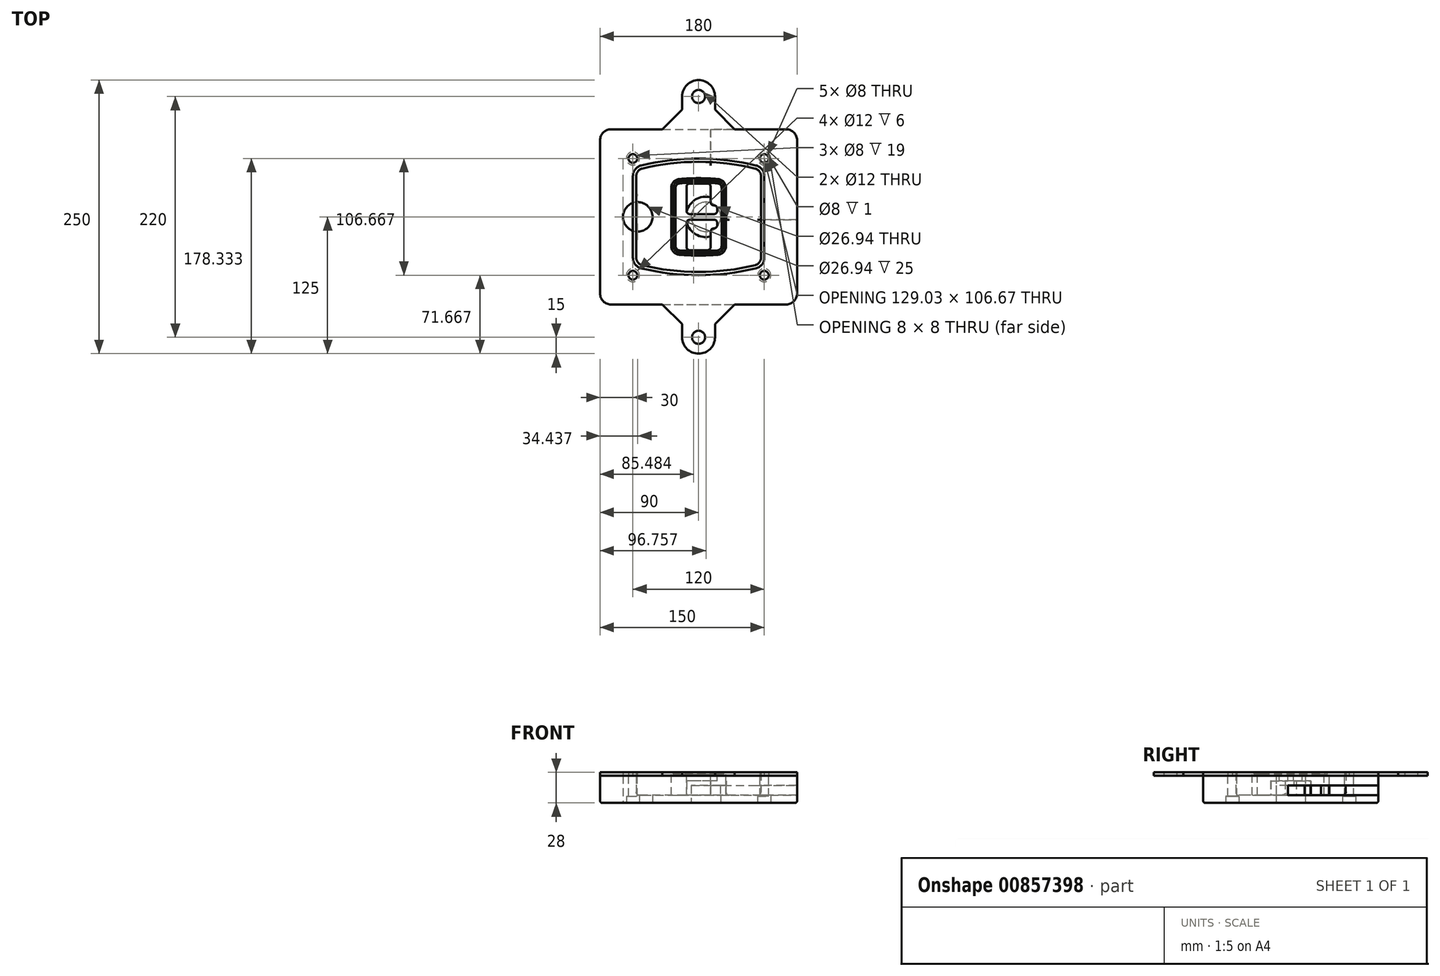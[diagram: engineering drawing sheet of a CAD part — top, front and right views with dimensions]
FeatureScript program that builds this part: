
annotation { "Feature Type Name" : "Feature", "Feature Type Description" : "" }
export const myFeature = defineFeature(function(context is Context, id is Id, definition is map)
    precondition{}
    {
        {
            var Q0;
            Q0=qCreatedBy(makeId("Top.planeOp"),FACE);
            var sketch = newSketch(context, id + "F0", { "sketchPlane" : qUnion([Q0])});
            skPoint(sketch, "E0.rect.middle", {"position": v(0, 0) * mm});
            skLineSegment(sketch, "E1.bottom", {"start": v(-80, -80) * mm, "end": v(80, -80) * mm});
            skLineSegment(sketch, "E1.top", {"start": v(-80, 80) * mm, "end": v(80, 80) * mm});
            skLineSegment(sketch, "E1.left", {"start": v(-90, -70) * mm, "end": v(-90, 70) * mm});
            skLineSegment(sketch, "E1.right", {"start": v(90, -70) * mm, "end": v(90, 70) * mm});
            skLineSegment(sketch, "E2", {"start": v(-90, 80) * mm, "end": v(90, -80) * mm, "construction": true});
            skLineSegment(sketch, "E3", {"start": v(90, 80) * mm, "end": v(-90, -80) * mm, "construction": true});
            skCircle(sketch, "E4", {"center": v(-60, 53.33) * mm, "radius": 4 * mm});
            skCircle(sketch, "E5", {"center": v(60, 53.33) * mm, "radius": 4 * mm});
            skCircle(sketch, "E6", {"center": v(60, -53.33) * mm, "radius": 4 * mm});
            skCircle(sketch, "E7", {"center": v(-60, -53.33) * mm, "radius": 4 * mm});
            skLineSegment(sketch, "E8", {"start": v(-60, 53.33) * mm, "end": v(60, 53.33) * mm, "construction": true});
            skLineSegment(sketch, "E9", {"start": v(60, 53.33) * mm, "end": v(60, -53.33) * mm, "construction": true});
            skLineSegment(sketch, "E10", {"start": v(60, -53.33) * mm, "end": v(-60, -53.33) * mm, "construction": true});
            skLineSegment(sketch, "E11", {"start": v(-60, -53.33) * mm, "end": v(-60, 53.33) * mm, "construction": true});
            skLineSegment(sketch, "E12", {"start": v(-60, 37.3) * mm, "end": v(-60, -37.3) * mm});
            skLineSegment(sketch, "E13", {"start": v(60, 37.3) * mm, "end": v(60, -37.3) * mm});
            skArc(sketch, "E14", {"start": v(52.38, 47.01) * mm, "mid": v(0, 53.33) * mm, "end": v(-52.38, 47.01) * mm});
            skArc(sketch, "E15", {"start": v(-52.38, -47.01) * mm, "mid": v(0, -53.33) * mm, "end": v(52.38, -47.01) * mm});
            skLineSegment(sketch, "E16", {"start": v(-60, 0) * mm, "end": v(60, 0) * mm, "construction": true});
            skPoint(sketch, "E17.visualSharp", {"position": v(-60, -45) * mm});
            skArc(sketch, "E17.filletArc", {"start": v(-60, -37.3) * mm, "mid": v(-57.87, -43.47) * mm, "end": v(-52.38, -47.01) * mm});
            skPoint(sketch, "E18.visualSharp", {"position": v(-60, 45) * mm});
            skArc(sketch, "E18.filletArc", {"start": v(-52.38, 47.01) * mm, "mid": v(-57.87, 43.47) * mm, "end": v(-60, 37.3) * mm});
            skPoint(sketch, "E19.visualSharp", {"position": v(60, 45) * mm});
            skArc(sketch, "E19.filletArc", {"start": v(60, 37.3) * mm, "mid": v(57.87, 43.47) * mm, "end": v(52.38, 47.01) * mm});
            skPoint(sketch, "E20.visualSharp", {"position": v(60, -45) * mm});
            skArc(sketch, "E20.filletArc", {"start": v(52.38, -47.01) * mm, "mid": v(57.87, -43.47) * mm, "end": v(60, -37.3) * mm});
            skPoint(sketch, "E21.visualSharp", {"position": v(-90, 80) * mm});
            skArc(sketch, "E21.filletArc", {"start": v(-80, 80) * mm, "mid": v(-87.07, 77.07) * mm, "end": v(-90, 70) * mm});
            skPoint(sketch, "E22.visualSharp", {"position": v(90, 80) * mm});
            skArc(sketch, "E22.filletArc", {"start": v(90, 70) * mm, "mid": v(87.07, 77.07) * mm, "end": v(80, 80) * mm});
            skPoint(sketch, "E23.visualSharp", {"position": v(90, -80) * mm});
            skArc(sketch, "E23.filletArc", {"start": v(80, -80) * mm, "mid": v(87.07, -77.07) * mm, "end": v(90, -70) * mm});
            skPoint(sketch, "E24.visualSharp", {"position": v(-90, -80) * mm});
            skArc(sketch, "E24.filletArc", {"start": v(-90, -70) * mm, "mid": v(-87.07, -77.07) * mm, "end": v(-80, -80) * mm});
            skArc(sketch, "E25.0", {"start": v(57, 37.3) * mm, "mid": v(55.5, 41.62) * mm, "end": v(51.67, 44.1) * mm});
            skLineSegment(sketch, "E25.1", {"start": v(57, 37.3) * mm, "end": v(57, -37.3) * mm});
            skArc(sketch, "E25.2", {"start": v(51.67, -44.1) * mm, "mid": v(55.5, -41.62) * mm, "end": v(57, -37.3) * mm});
            skArc(sketch, "E25.3", {"start": v(-51.67, -44.1) * mm, "mid": v(0, -50.33) * mm, "end": v(51.67, -44.1) * mm});
            skArc(sketch, "E25.4", {"start": v(-57, -37.3) * mm, "mid": v(-55.5, -41.62) * mm, "end": v(-51.67, -44.1) * mm});
            skArc(sketch, "E25.5", {"start": v(51.67, 44.1) * mm, "mid": v(0, 50.33) * mm, "end": v(-51.67, 44.1) * mm});
            skLineSegment(sketch, "E25.6", {"start": v(-57, 37.3) * mm, "end": v(-57, -37.3) * mm});
            skArc(sketch, "E25.7", {"start": v(-51.67, 44.1) * mm, "mid": v(-55.5, 41.62) * mm, "end": v(-57, 37.3) * mm});
            skArc(sketch, "E26.0", {"start": v(-53.33, 50.9) * mm, "mid": v(-61.01, 45.94) * mm, "end": v(-64, 37.3) * mm});
            skArc(sketch, "E26.1", {"start": v(53.33, 50.9) * mm, "mid": v(0, 57.33) * mm, "end": v(-53.33, 50.9) * mm});
            skArc(sketch, "E26.2", {"start": v(64, 37.3) * mm, "mid": v(61.01, 45.94) * mm, "end": v(53.33, 50.9) * mm});
            skLineSegment(sketch, "E26.3", {"start": v(64, 37.3) * mm, "end": v(64, -37.3) * mm});
            skArc(sketch, "E26.4", {"start": v(53.33, -50.9) * mm, "mid": v(61.01, -45.94) * mm, "end": v(64, -37.3) * mm});
            skLineSegment(sketch, "E26.5", {"start": v(-64, 37.3) * mm, "end": v(-64, -37.3) * mm});
            skArc(sketch, "E26.6", {"start": v(-53.33, -50.9) * mm, "mid": v(0, -57.33) * mm, "end": v(53.33, -50.9) * mm});
            skArc(sketch, "E26.7", {"start": v(-64, -37.3) * mm, "mid": v(-61.01, -45.94) * mm, "end": v(-53.33, -50.9) * mm});
            skSolve(sketch);
        }
        {
            var Q0;
            Q0=makeQuery(id+"F0.imprint","IMPRINT",FACE,{"disambiguationData":[TD([[makeQuery(id+"F0.imprint","IMPRINT",EDGE,{"derivedFrom":sQuery(id+"F0.wireOp",EDGE,"E1.bottom")}),1.0]])]});
            var Q1;
            Q1=makeQuery(id+"F0.imprint","IMPRINT",FACE,{"disambiguationData":[TD([[makeQuery(id+"F0.imprint","IMPRINT",EDGE,{"derivedFrom":sQuery(id+"F0.wireOp",EDGE,"E12")}),1.0]])]});
            var Q2;
            Q2=makeQuery(id+"F0.imprint","IMPRINT",FACE,{"disambiguationData":[TD([[makeQuery(id+"F0.imprint","IMPRINT",EDGE,{"derivedFrom":sQuery(id+"F0.wireOp",EDGE,"E25.0")}),1.0]])]});
            var Q3;
            Q3=makeQuery(id+"F0.imprint","IMPRINT",FACE,{"disambiguationData":[TD([[makeQuery(id+"F0.imprint","IMPRINT",EDGE,{"derivedFrom":sQuery(id+"F0.wireOp",EDGE,"E12")}),-1.0]])]});
            extrude(context, id + "F1", {"entities" : qUnion([Q0, Q1, Q2, Q3]), "oppositeDirection" : true, "depth" : 25 * mm});
        }
        {
            var Q0;
            Q0=makeQuery(id+"F0.imprint","IMPRINT",FACE,{"disambiguationData":[TD([[makeQuery(id+"F0.imprint","IMPRINT",EDGE,{"derivedFrom":sQuery(id+"F0.wireOp",EDGE,"E12")}),1.0]])]});
            extrude(context, id + "F2", {"entities" : qUnion([Q0]), "operationType" : NewBodyOperationType.ADD, "depth" : 3 * mm});
        }
        {
            var Q0;
            Q0=makeQuery(id+"F0.imprint","IMPRINT",FACE,{"disambiguationData":[TD([[makeQuery(id+"F0.imprint","IMPRINT",EDGE,{"derivedFrom":sQuery(id+"F0.wireOp",EDGE,"E25.0")}),1.0]])]});
            extrude(context, id + "F3", {"entities" : qUnion([Q0]), "operationType" : NewBodyOperationType.REMOVE, "oppositeDirection" : true, "depth" : 18 * mm});
        }
        {
            var Q0;
            Q0=makeQuery(id+"F2.opExtrude","CAP_FACE",FACE,{"disambiguationData":[OSD([sQuery(id+"F0.wireOp",EDGE,"E12"),sQuery(id+"F0.wireOp",EDGE,"E13"),sQuery(id+"F0.wireOp",EDGE,"E14"),sQuery(id+"F0.wireOp",EDGE,"E15"),sQuery(id+"F0.wireOp",EDGE,"E17.filletArc"),sQuery(id+"F0.wireOp",EDGE,"E18.filletArc"),sQuery(id+"F0.wireOp",EDGE,"E19.filletArc"),sQuery(id+"F0.wireOp",EDGE,"E20.filletArc"),sQuery(id+"F0.wireOp",EDGE,"E25.0"),sQuery(id+"F0.wireOp",EDGE,"E25.1"),sQuery(id+"F0.wireOp",EDGE,"E25.2"),sQuery(id+"F0.wireOp",EDGE,"E25.3"),sQuery(id+"F0.wireOp",EDGE,"E25.4"),sQuery(id+"F0.wireOp",EDGE,"E25.5"),sQuery(id+"F0.wireOp",EDGE,"E25.6"),sQuery(id+"F0.wireOp",EDGE,"E25.7")])],"isStart":false});
            var sketch = newSketch(context, id + "F4", { "sketchPlane" : qUnion([Q0])});
            skArc(sketch, "E27.0", {"start": v(-17.7, -34.56) * mm, "mid": v(0, -35.33) * mm, "end": v(17.7, -34.56) * mm});
            skArc(sketch, "E28.0", {"start": v(17.7, 34.56) * mm, "mid": v(0, 35.33) * mm, "end": v(-17.7, 34.56) * mm});
            skLineSegment(sketch, "E29", {"start": v(-25, 26.59) * mm, "end": v(-25, -26.59) * mm});
            skLineSegment(sketch, "E30", {"start": v(25, 26.59) * mm, "end": v(25, -26.59) * mm});
            skLineSegment(sketch, "E31", {"start": v(-25, 33.78) * mm, "end": v(25, 33.78) * mm, "construction": true});
            skLineSegment(sketch, "E32", {"start": v(-25, -33.78) * mm, "end": v(25, -33.78) * mm, "construction": true});
            skPoint(sketch, "E33.visualSharp", {"position": v(-25, 33.78) * mm});
            skArc(sketch, "E33.filletArc", {"start": v(-17.7, 34.56) * mm, "mid": v(-22.9, 32) * mm, "end": v(-25, 26.59) * mm});
            skPoint(sketch, "E34.visualSharp", {"position": v(25, 33.78) * mm});
            skArc(sketch, "E34.filletArc", {"start": v(25, 26.59) * mm, "mid": v(22.9, 32) * mm, "end": v(17.7, 34.56) * mm});
            skPoint(sketch, "E35.visualSharp", {"position": v(25, -33.78) * mm});
            skArc(sketch, "E35.filletArc", {"start": v(17.7, -34.56) * mm, "mid": v(22.9, -32) * mm, "end": v(25, -26.59) * mm});
            skPoint(sketch, "E36.visualSharp", {"position": v(-25, -33.78) * mm});
            skArc(sketch, "E36.filletArc", {"start": v(-25, -26.59) * mm, "mid": v(-22.9, -32) * mm, "end": v(-17.7, -34.56) * mm});
            skArc(sketch, "E37.0", {"start": v(51.67, 44.1) * mm, "mid": v(0, 50.33) * mm, "end": v(-51.67, 44.1) * mm});
            skArc(sketch, "E37.1", {"start": v(-51.67, 44.1) * mm, "mid": v(-55.5, 41.62) * mm, "end": v(-57, 37.3) * mm});
            skLineSegment(sketch, "E37.2", {"start": v(-57, 37.3) * mm, "end": v(-57, -37.3) * mm});
            skArc(sketch, "E37.3", {"start": v(-57, -37.3) * mm, "mid": v(-55.5, -41.62) * mm, "end": v(-51.67, -44.1) * mm});
            skArc(sketch, "E37.4", {"start": v(-51.67, -44.1) * mm, "mid": v(0, -50.33) * mm, "end": v(51.67, -44.1) * mm});
            skArc(sketch, "E37.5", {"start": v(51.67, -44.1) * mm, "mid": v(55.5, -41.62) * mm, "end": v(57, -37.3) * mm});
            skLineSegment(sketch, "E37.6", {"start": v(57, 37.3) * mm, "end": v(57, -37.3) * mm});
            skArc(sketch, "E37.7", {"start": v(57, 37.3) * mm, "mid": v(55.5, 41.62) * mm, "end": v(51.67, 44.1) * mm});
            skLineSegment(sketch, "E38.0", {"start": v(23, 26.59) * mm, "end": v(23, -26.59) * mm});
            skArc(sketch, "E38.1", {"start": v(17.53, -32.56) * mm, "mid": v(21.42, -30.64) * mm, "end": v(23, -26.59) * mm});
            skArc(sketch, "E38.2", {"start": v(-17.53, -32.56) * mm, "mid": v(0, -33.33) * mm, "end": v(17.53, -32.56) * mm});
            skArc(sketch, "E38.3", {"start": v(-23, -26.59) * mm, "mid": v(-21.42, -30.64) * mm, "end": v(-17.53, -32.56) * mm});
            skLineSegment(sketch, "E38.4", {"start": v(-23, 26.59) * mm, "end": v(-23, -26.59) * mm});
            skArc(sketch, "E38.5", {"start": v(23, 26.59) * mm, "mid": v(21.42, 30.64) * mm, "end": v(17.53, 32.56) * mm});
            skArc(sketch, "E38.6", {"start": v(-17.53, 32.56) * mm, "mid": v(-21.42, 30.64) * mm, "end": v(-23, 26.59) * mm});
            skArc(sketch, "E38.7", {"start": v(17.53, 32.56) * mm, "mid": v(0, 33.33) * mm, "end": v(-17.53, 32.56) * mm});
            skArc(sketch, "E39.0", {"start": v(21, 26.59) * mm, "mid": v(19.95, 29.29) * mm, "end": v(17.35, 30.57) * mm});
            skLineSegment(sketch, "E39.1", {"start": v(21, 26.59) * mm, "end": v(21, -26.59) * mm});
            skArc(sketch, "E39.2", {"start": v(17.35, -30.57) * mm, "mid": v(19.95, -29.29) * mm, "end": v(21, -26.59) * mm});
            skArc(sketch, "E39.3", {"start": v(-17.35, -30.57) * mm, "mid": v(0, -31.33) * mm, "end": v(17.35, -30.57) * mm});
            skArc(sketch, "E39.4", {"start": v(-21, -26.59) * mm, "mid": v(-19.95, -29.29) * mm, "end": v(-17.35, -30.57) * mm});
            skArc(sketch, "E39.5", {"start": v(17.35, 30.57) * mm, "mid": v(0, 31.33) * mm, "end": v(-17.35, 30.57) * mm});
            skLineSegment(sketch, "E39.6", {"start": v(-21, 26.59) * mm, "end": v(-21, -26.59) * mm});
            skArc(sketch, "E39.7", {"start": v(-17.35, 30.57) * mm, "mid": v(-19.95, 29.29) * mm, "end": v(-21, 26.59) * mm});
            skLineSegment(sketch, "E40", {"start": v(-25, 0) * mm, "end": v(25, 0) * mm, "construction": true});
            skLineSegment(sketch, "E41", {"start": v(-11, 5.5) * mm, "end": v(-11, 27.5) * mm});
            skLineSegment(sketch, "E42", {"start": v(-8, 30.5) * mm, "end": v(8, 30.5) * mm});
            skLineSegment(sketch, "E43", {"start": v(11, 27.5) * mm, "end": v(11, 13.5) * mm});
            skLineSegment(sketch, "E44", {"start": v(14, 10.5) * mm, "end": v(14, 10.5) * mm});
            skLineSegment(sketch, "E45", {"start": v(17, 7.5) * mm, "end": v(17, 5.5) * mm});
            skLineSegment(sketch, "E46", {"start": v(14, 2.5) * mm, "end": v(-8, 2.5) * mm});
            skPoint(sketch, "E47.visualSharp", {"position": v(-11, 30.5) * mm});
            skArc(sketch, "E47.filletArc", {"start": v(-8, 30.5) * mm, "mid": v(-10.12, 29.62) * mm, "end": v(-11, 27.5) * mm});
            skPoint(sketch, "E48.visualSharp", {"position": v(11, 30.5) * mm});
            skArc(sketch, "E48.filletArc", {"start": v(11, 27.5) * mm, "mid": v(10.12, 29.62) * mm, "end": v(8, 30.5) * mm});
            skPoint(sketch, "E49.visualSharp", {"position": v(11, 10.5) * mm});
            skArc(sketch, "E49.filletArc", {"start": v(11, 13.5) * mm, "mid": v(11.88, 11.38) * mm, "end": v(14, 10.5) * mm});
            skPoint(sketch, "E50.visualSharp", {"position": v(17, 10.5) * mm});
            skArc(sketch, "E50.filletArc", {"start": v(17, 7.5) * mm, "mid": v(16.12, 9.62) * mm, "end": v(14, 10.5) * mm});
            skPoint(sketch, "E51.visualSharp", {"position": v(17, 2.5) * mm});
            skArc(sketch, "E51.filletArc", {"start": v(14, 2.5) * mm, "mid": v(16.12, 3.38) * mm, "end": v(17, 5.5) * mm});
            skPoint(sketch, "E52.visualSharp", {"position": v(-11, 2.5) * mm});
            skArc(sketch, "E52.filletArc", {"start": v(-11, 5.5) * mm, "mid": v(-10.12, 3.38) * mm, "end": v(-8, 2.5) * mm});
            skLineSegment(sketch, "E53.0.MirrorCS", {"start": v(14, -2.5) * mm, "end": v(-8, -2.5) * mm});
            skArc(sketch, "E54.0.MirrorCS", {"start": v(-11, -5.5) * mm, "mid": v(-10.12, -3.38) * mm, "end": v(-8, -2.5) * mm});
            skLineSegment(sketch, "E55.0.MirrorCS", {"start": v(-11, -5.5) * mm, "end": v(-11, -27.5) * mm});
            skArc(sketch, "E56.0.MirrorCS", {"start": v(-8, -30.5) * mm, "mid": v(-10.12, -29.62) * mm, "end": v(-11, -27.5) * mm});
            skLineSegment(sketch, "E57.0.MirrorCS", {"start": v(-8, -30.5) * mm, "end": v(8, -30.5) * mm});
            skArc(sketch, "E58.0.MirrorCS", {"start": v(11, -27.5) * mm, "mid": v(10.12, -29.62) * mm, "end": v(8, -30.5) * mm});
            skLineSegment(sketch, "E59.0.MirrorCS", {"start": v(11, -27.5) * mm, "end": v(11, -13.5) * mm});
            skArc(sketch, "E60.0.MirrorCS", {"start": v(11, -13.5) * mm, "mid": v(11.88, -11.38) * mm, "end": v(14, -10.5) * mm});
            skArc(sketch, "E61.0.MirrorCS", {"start": v(17, -7.5) * mm, "mid": v(16.12, -9.62) * mm, "end": v(14, -10.5) * mm});
            skLineSegment(sketch, "E62.0.MirrorCS", {"start": v(17, -7.5) * mm, "end": v(17, -5.5) * mm});
            skArc(sketch, "E63.0.MirrorCS", {"start": v(14, -2.5) * mm, "mid": v(16.12, -3.38) * mm, "end": v(17, -5.5) * mm});
            skSolve(sketch);
        }
        {
            var Q0;
            Q0=makeQuery(id+"F4.imprint","IMPRINT",FACE,{"disambiguationData":[TD([[makeQuery(id+"F4.imprint","IMPRINT",EDGE,{"derivedFrom":sQuery(id+"F4.wireOp",EDGE,"E27.0")}),1.0]])]});
            var Q1;
            Q1=makeQuery(id+"F4.imprint","IMPRINT",FACE,{"disambiguationData":[TD([[makeQuery(id+"F4.imprint","IMPRINT",EDGE,{"derivedFrom":sQuery(id+"F4.wireOp",EDGE,"E38.0")}),-1.0]])]});
            var Q2;
            Q2=makeQuery(id+"F4.imprint","IMPRINT",FACE,{"disambiguationData":[TD([[makeQuery(id+"F4.imprint","IMPRINT",EDGE,{"derivedFrom":sQuery(id+"F4.wireOp",EDGE,"E39.0")}),1.0]])]});
            extrude(context, id + "F5", {"entities" : qUnion([Q0, Q1, Q2]), "operationType" : NewBodyOperationType.ADD, "endBound" : BoundingType.UP_TO_NEXT, "oppositeDirection" : true, "depth" : 25 * mm});
        }
        {
            var Q0;
            Q0=makeQuery(id+"F4.imprint","IMPRINT",FACE,{"disambiguationData":[TD([[makeQuery(id+"F4.imprint","IMPRINT",EDGE,{"derivedFrom":sQuery(id+"F4.wireOp",EDGE,"E38.0")}),-1.0]])]});
            extrude(context, id + "F6", {"entities" : qUnion([Q0]), "operationType" : NewBodyOperationType.REMOVE, "oppositeDirection" : true, "depth" : 2 * mm});
        }
        {
            var Q0;
            Q0=makeQuery(id+"F1.opExtrude","CAP_FACE",FACE,{"disambiguationData":[OSD([sQuery(id+"F0.wireOp",EDGE,"E1.bottom"),sQuery(id+"F0.wireOp",EDGE,"E1.top"),sQuery(id+"F0.wireOp",EDGE,"E1.left"),sQuery(id+"F0.wireOp",EDGE,"E1.right"),sQuery(id+"F0.wireOp",EDGE,"E4"),sQuery(id+"F0.wireOp",EDGE,"E5"),sQuery(id+"F0.wireOp",EDGE,"E6"),sQuery(id+"F0.wireOp",EDGE,"E7"),sQuery(id+"F0.wireOp",EDGE,"E21.filletArc"),sQuery(id+"F0.wireOp",EDGE,"E22.filletArc"),sQuery(id+"F0.wireOp",EDGE,"E23.filletArc"),sQuery(id+"F0.wireOp",EDGE,"E24.filletArc")])],"isStart":false});
            var sketch = newSketch(context, id + "F7", { "sketchPlane" : qUnion([Q0])});
            skCircle(sketch, "E64", {"center": v(6.76, 0) * mm, "radius": 13.47 * mm});
            skCircle(sketch, "E65", {"center": v(-55.56, 0) * mm, "radius": 13.47 * mm});
            skLineSegment(sketch, "E66", {"start": v(90, 0) * mm, "end": v(-90, 0) * mm});
            skCircle(sketch, "E67", {"center": v(6.76, 0) * mm, "radius": 18.47 * mm});
            skCircle(sketch, "E68", {"center": v(60, -53.33) * mm, "radius": 6 * mm});
            skCircle(sketch, "E69", {"center": v(-60, -53.33) * mm, "radius": 6 * mm});
            skCircle(sketch, "E70", {"center": v(-60, 53.33) * mm, "radius": 6 * mm});
            skCircle(sketch, "E71", {"center": v(60, 53.33) * mm, "radius": 6 * mm});
            skSolve(sketch);
        }
        {
            var Q0;
            {var subQ1=sQuery(id+"F7.wireOp",EDGE,"E66");var subQ4=sQuery(id+"F7.wireOp",EDGE,"E64");var subQ6=makeQuery(id+"F7.imprint","INTERSECT",VERTEX,{"disambiguationData":[OD(0.0)],"derivedFrom":[subQ4,subQ1]});Q0=makeQuery(id+"F7.imprint","IMPRINT",FACE,{"disambiguationData":[TD([[makeQuery(id+"F7.imprint","IMPRINT",EDGE,{"disambiguationData":[TD([[subQ6,-1.0]])],"derivedFrom":subQ4}),-1.0]])]});}
            var Q1;
            {var subQ0=sQuery(id+"F7.wireOp",EDGE,"E66");var subQ1=sQuery(id+"F7.wireOp",EDGE,"E64");var subQ3=makeQuery(id+"F7.imprint","INTERSECT",VERTEX,{"disambiguationData":[OD(0.0)],"derivedFrom":[subQ1,subQ0]});Q1=makeQuery(id+"F7.imprint","IMPRINT",FACE,{"disambiguationData":[TD([[makeQuery(id+"F7.imprint","IMPRINT",EDGE,{"disambiguationData":[TD([[subQ3,-1.0]])],"derivedFrom":subQ1}),1.0]])]});}
            var Q2;
            {var subQ0=sQuery(id+"F7.wireOp",EDGE,"E66");var subQ1=sQuery(id+"F7.wireOp",EDGE,"E64");var subQ3=makeQuery(id+"F7.imprint","INTERSECT",VERTEX,{"disambiguationData":[OD(0.0)],"derivedFrom":[subQ1,subQ0]});Q2=makeQuery(id+"F7.imprint","IMPRINT",FACE,{"disambiguationData":[TD([[makeQuery(id+"F7.imprint","IMPRINT",EDGE,{"disambiguationData":[TD([[subQ3,1.0]])],"derivedFrom":subQ1}),1.0]])]});}
            var Q3;
            {var subQ1=sQuery(id+"F7.wireOp",EDGE,"E66");var subQ4=sQuery(id+"F7.wireOp",EDGE,"E64");var subQ6=makeQuery(id+"F7.imprint","INTERSECT",VERTEX,{"disambiguationData":[OD(0.0)],"derivedFrom":[subQ4,subQ1]});Q3=makeQuery(id+"F7.imprint","IMPRINT",FACE,{"disambiguationData":[TD([[makeQuery(id+"F7.imprint","IMPRINT",EDGE,{"disambiguationData":[TD([[subQ6,1.0]])],"derivedFrom":subQ4}),-1.0]])]});}
            extrude(context, id + "F8", {"entities" : qUnion([Q0, Q1, Q2, Q3]), "operationType" : NewBodyOperationType.ADD, "oppositeDirection" : true, "depth" : 20 * mm});
        }
        {
            var Q0;
            {var subQ0=sQuery(id+"F7.wireOp",EDGE,"E66");var subQ1=sQuery(id+"F7.wireOp",EDGE,"E64");var subQ3=makeQuery(id+"F7.imprint","INTERSECT",VERTEX,{"disambiguationData":[OD(0.0)],"derivedFrom":[subQ1,subQ0]});Q0=makeQuery(id+"F7.imprint","IMPRINT",FACE,{"disambiguationData":[TD([[makeQuery(id+"F7.imprint","IMPRINT",EDGE,{"disambiguationData":[TD([[subQ3,-1.0]])],"derivedFrom":subQ1}),1.0]])]});}
            var Q1;
            {var subQ0=sQuery(id+"F7.wireOp",EDGE,"E66");var subQ1=sQuery(id+"F7.wireOp",EDGE,"E64");var subQ3=makeQuery(id+"F7.imprint","INTERSECT",VERTEX,{"disambiguationData":[OD(0.0)],"derivedFrom":[subQ1,subQ0]});Q1=makeQuery(id+"F7.imprint","IMPRINT",FACE,{"disambiguationData":[TD([[makeQuery(id+"F7.imprint","IMPRINT",EDGE,{"disambiguationData":[TD([[subQ3,1.0]])],"derivedFrom":subQ1}),1.0]])]});}
            extrude(context, id + "F9", {"entities" : qUnion([Q0, Q1]), "operationType" : NewBodyOperationType.REMOVE, "oppositeDirection" : true, "depth" : 16 * mm});
        }
        {
            var Q0;
            {var subQ0=sQuery(id+"F7.wireOp",EDGE,"E66");var subQ1=sQuery(id+"F7.wireOp",EDGE,"E65");var subQ3=makeQuery(id+"F7.imprint","INTERSECT",VERTEX,{"disambiguationData":[OD(0.0)],"derivedFrom":[subQ1,subQ0]});Q0=makeQuery(id+"F7.imprint","IMPRINT",FACE,{"disambiguationData":[TD([[makeQuery(id+"F7.imprint","IMPRINT",EDGE,{"disambiguationData":[TD([[subQ3,-1.0]])],"derivedFrom":subQ1}),1.0]])]});}
            var Q1;
            {var subQ0=sQuery(id+"F7.wireOp",EDGE,"E66");var subQ1=sQuery(id+"F7.wireOp",EDGE,"E65");var subQ3=makeQuery(id+"F7.imprint","INTERSECT",VERTEX,{"disambiguationData":[OD(0.0)],"derivedFrom":[subQ1,subQ0]});Q1=makeQuery(id+"F7.imprint","IMPRINT",FACE,{"disambiguationData":[TD([[makeQuery(id+"F7.imprint","IMPRINT",EDGE,{"disambiguationData":[TD([[subQ3,1.0]])],"derivedFrom":subQ1}),1.0]])]});}
            extrude(context, id + "F10", {"entities" : qUnion([Q0, Q1]), "operationType" : NewBodyOperationType.REMOVE, "oppositeDirection" : true, "depth" : 25 * mm});
        }
        {
            var Q0;
            Q0=makeQuery(id+"F7.imprint","IMPRINT",FACE,{"disambiguationData":[TD([[makeQuery(id+"F7.imprint","IMPRINT",EDGE,{"derivedFrom":sQuery(id+"F7.wireOp",EDGE,"E68")}),1.0]])]});
            var Q1;
            Q1=makeQuery(id+"F7.imprint","IMPRINT",FACE,{"disambiguationData":[TD([[makeQuery(id+"F7.imprint","IMPRINT",EDGE,{"derivedFrom":makeQuery(id+"F1.opExtrude","CAP_EDGE",EDGE,{"disambiguationData":[OSD([sQuery(id+"F0.wireOp",EDGE,"E5")])],"isStart":false})}),-1.0]])]});
            var Q2;
            Q2=makeQuery(id+"F7.imprint","IMPRINT",FACE,{"disambiguationData":[TD([[makeQuery(id+"F7.imprint","IMPRINT",EDGE,{"derivedFrom":sQuery(id+"F7.wireOp",EDGE,"E69")}),1.0]])]});
            var Q3;
            Q3=makeQuery(id+"F7.imprint","IMPRINT",FACE,{"disambiguationData":[TD([[makeQuery(id+"F7.imprint","IMPRINT",EDGE,{"derivedFrom":makeQuery(id+"F1.opExtrude","CAP_EDGE",EDGE,{"disambiguationData":[OSD([sQuery(id+"F0.wireOp",EDGE,"E4")])],"isStart":false})}),-1.0]])]});
            var Q4;
            Q4=makeQuery(id+"F7.imprint","IMPRINT",FACE,{"disambiguationData":[TD([[makeQuery(id+"F7.imprint","IMPRINT",EDGE,{"derivedFrom":sQuery(id+"F7.wireOp",EDGE,"E70")}),1.0]])]});
            var Q5;
            Q5=makeQuery(id+"F7.imprint","IMPRINT",FACE,{"disambiguationData":[TD([[makeQuery(id+"F7.imprint","IMPRINT",EDGE,{"derivedFrom":makeQuery(id+"F1.opExtrude","CAP_EDGE",EDGE,{"disambiguationData":[OSD([sQuery(id+"F0.wireOp",EDGE,"E7")])],"isStart":false})}),-1.0]])]});
            var Q6;
            Q6=makeQuery(id+"F7.imprint","IMPRINT",FACE,{"disambiguationData":[TD([[makeQuery(id+"F7.imprint","IMPRINT",EDGE,{"derivedFrom":sQuery(id+"F7.wireOp",EDGE,"E71")}),1.0]])]});
            var Q7;
            Q7=makeQuery(id+"F7.imprint","IMPRINT",FACE,{"disambiguationData":[TD([[makeQuery(id+"F7.imprint","IMPRINT",EDGE,{"derivedFrom":makeQuery(id+"F1.opExtrude","CAP_EDGE",EDGE,{"disambiguationData":[OSD([sQuery(id+"F0.wireOp",EDGE,"E6")])],"isStart":false})}),-1.0]])]});
            extrude(context, id + "F11", {"entities" : qUnion([Q0, Q1, Q2, Q3, Q4, Q5, Q6, Q7]), "operationType" : NewBodyOperationType.REMOVE, "oppositeDirection" : true, "depth" : 6 * mm});
        }
        {
            var Q0;
            Q0=makeQuery(id+"F9.boolean.opBoolean","COPY",FACE,{"derivedFrom":makeQuery(id+"F9.opExtrude","CAP_FACE",FACE,{"disambiguationData":[OSD([sQuery(id+"F7.wireOp",EDGE,"E64")])],"isStart":false})});
            var sketch = newSketch(context, id + "F12", { "sketchPlane" : qUnion([Q0])});
            skArc(sketch, "E72.0", {"start": v(11, -88.19) * mm, "mid": v(97.1, -83.6) * mm, "end": v(92.5, 2.5) * mm});
            skLineSegment(sketch, "E72.1", {"start": v(11, -17.97) * mm, "end": v(11, -17.97) * mm});
            skLineSegment(sketch, "E73", {"start": v(92.5, -105.13) * mm, "end": v(102.3, -105.13) * mm});
            skLineSegment(sketch, "E74.0", {"start": v(92.5, 2.5) * mm, "end": v(14, 2.5) * mm});
            skArc(sketch, "E74.1", {"start": v(14, 2.5) * mm, "mid": v(16.12, 3.38) * mm, "end": v(17, 5.5) * mm});
            skLineSegment(sketch, "E74.2", {"start": v(17, 7.5) * mm, "end": v(17, 5.5) * mm});
            skArc(sketch, "E74.3", {"start": v(17, 7.5) * mm, "mid": v(16.12, 9.62) * mm, "end": v(14, 10.5) * mm});
            skArc(sketch, "E74.4", {"start": v(11, 13.5) * mm, "mid": v(11.88, 11.38) * mm, "end": v(14, 10.5) * mm});
            skLineSegment(sketch, "E74.5", {"start": v(11, 13.5) * mm, "end": v(11, -88.19) * mm});
            skLineSegment(sketch, "E74.7", {"start": v(92.5, -2.5) * mm, "end": v(14, -2.5) * mm});
            skArc(sketch, "E74.8", {"start": v(14, -2.5) * mm, "mid": v(16.12, -3.38) * mm, "end": v(17, -5.5) * mm});
            skLineSegment(sketch, "E74.9", {"start": v(17, -7.5) * mm, "end": v(17, -5.5) * mm});
            skArc(sketch, "E74.10", {"start": v(17, -7.5) * mm, "mid": v(16.12, -9.62) * mm, "end": v(14, -10.5) * mm});
            skArc(sketch, "E74.11", {"start": v(11, -13.5) * mm, "mid": v(11.88, -11.38) * mm, "end": v(14, -10.5) * mm});
            skLineSegment(sketch, "E74.12", {"start": v(11, -17.97) * mm, "end": v(11, -13.5) * mm});
            skPoint(sketch, "E75.orphan", {"position": v(11, -27.5) * mm});
            skPoint(sketch, "E76.orphan", {"position": v(-8, -2.5) * mm});
            skPoint(sketch, "E77.orphan", {"position": v(-8, 2.5) * mm});
            skPoint(sketch, "E78.orphan", {"position": v(11, 27.5) * mm});
            skSolve(sketch);
        }
        {
            var Q0;
            {var subQ7=sQuery(id+"F12.wireOp",EDGE,"E72.0");var subQ14=sQuery(id+"F12.wireOp",EDGE,"E72.1");var subQ16=sQuery(id+"F12.wireOp",EDGE,"E74.1");var subQ18=sQuery(id+"F12.wireOp",EDGE,"E74.8");Q0=qUnion([makeQuery(id+"F12.imprint","IMPRINT",FACE,{"disambiguationData":[TD([[makeQuery(id+"F12.imprint","IMPRINT",EDGE,{"derivedFrom":subQ7}),1.0]])]}),makeQuery(id+"F12.imprint","IMPRINT",FACE,{"disambiguationData":[TD([[makeQuery(id+"F12.imprint","IMPRINT",EDGE,{"derivedFrom":subQ14}),1.0]])]}),makeQuery(id+"F12.imprint","IMPRINT",FACE,{"disambiguationData":[TD([[makeQuery(id+"F12.imprint","IMPRINT",EDGE,{"derivedFrom":subQ16}),1.0]])]}),makeQuery(id+"F12.imprint","IMPRINT",FACE,{"disambiguationData":[TD([[makeQuery(id+"F12.imprint","IMPRINT",EDGE,{"derivedFrom":subQ18}),-1.0]])]})]);}
            var Q1;
            Q1=makeQuery(id+"F5.boolean.opBoolean","SPLIT",FACE,{"disambiguationData":[TD([makeQuery(id+"F5.opExtrude","SWEPT_FACE",FACE,{"disambiguationData":[OSD([sQuery(id+"F4.wireOp",EDGE,"E41")])]})])],"derivedFrom":makeQuery(id+"F3.boolean.opBoolean","COPY",FACE,{"derivedFrom":makeQuery(id+"F3.opExtrude","CAP_FACE",FACE,{"disambiguationData":[OSD([sQuery(id+"F0.wireOp",EDGE,"E25.0"),sQuery(id+"F0.wireOp",EDGE,"E25.1"),sQuery(id+"F0.wireOp",EDGE,"E25.2"),sQuery(id+"F0.wireOp",EDGE,"E25.3"),sQuery(id+"F0.wireOp",EDGE,"E25.4"),sQuery(id+"F0.wireOp",EDGE,"E25.5"),sQuery(id+"F0.wireOp",EDGE,"E25.6"),sQuery(id+"F0.wireOp",EDGE,"E25.7")])],"isStart":false})})});
            extrude(context, id + "F13", {"entities" : qUnion([Q0]), "operationType" : NewBodyOperationType.REMOVE, "endBound" : BoundingType.UP_TO_SURFACE, "endBoundEntityFace" : qUnion([Q1]), "depth" : 25 * mm});
        }
        {
            var Q0;
            Q0=makeQuery(id+"F3.boolean.opBoolean","COPY",EDGE,{"derivedFrom":makeQuery(id+"F3.opExtrude","CAP_EDGE",EDGE,{"disambiguationData":[OSD([sQuery(id+"F0.wireOp",EDGE,"E25.6")])],"isStart":false})});
            var Q1;
            Q1=makeQuery(id+"F8.boolean.opBoolean","INTERSECT",EDGE,{"derivedFrom":[makeQuery(id+"F5.opExtrude","SWEPT_FACE",FACE,{"disambiguationData":[OSD([sQuery(id+"F4.wireOp",EDGE,"E30")])]}),makeQuery(id+"F8.opExtrude","CAP_FACE",FACE,{"disambiguationData":[OSD([sQuery(id+"F7.wireOp",EDGE,"E67")])],"isStart":false})]});
            var Q2;
            Q2=makeQuery(id+"F8.boolean.opBoolean","INTERSECT",EDGE,{"disambiguationData":[OD(1.0)],"derivedFrom":[makeQuery(id+"F5.opExtrude","SWEPT_FACE",FACE,{"disambiguationData":[OSD([sQuery(id+"F4.wireOp",EDGE,"E30")])]}),makeQuery(id+"F8.opExtrude","SWEPT_FACE",FACE,{"disambiguationData":[OSD([sQuery(id+"F7.wireOp",EDGE,"E67")])]})]});
            var Q3;
            {var subQ0=makeQuery(id+"F3.boolean.opBoolean","COPY",FACE,{"derivedFrom":makeQuery(id+"F3.opExtrude","CAP_FACE",FACE,{"disambiguationData":[OSD([sQuery(id+"F0.wireOp",EDGE,"E25.0"),sQuery(id+"F0.wireOp",EDGE,"E25.1"),sQuery(id+"F0.wireOp",EDGE,"E25.2"),sQuery(id+"F0.wireOp",EDGE,"E25.3"),sQuery(id+"F0.wireOp",EDGE,"E25.4"),sQuery(id+"F0.wireOp",EDGE,"E25.5"),sQuery(id+"F0.wireOp",EDGE,"E25.6"),sQuery(id+"F0.wireOp",EDGE,"E25.7")])],"isStart":false})});var subQ1=sQuery(id+"F4.wireOp",EDGE,"E30");Q3=makeQuery(id+"F8.boolean.opBoolean","SPLIT",EDGE,{"disambiguationData":[TD([makeQuery(id+"F5.opExtrude","SWEPT_FACE",FACE,{"disambiguationData":[OSD([sQuery(id+"F4.wireOp",EDGE,"E35.filletArc")])]})])],"derivedFrom":makeQuery(id+"F5.opExtrude","TWEAK_EDGE",EDGE,{"derivedFrom":[subQ0,makeQuery(id+"F4.imprint","IMPRINT",EDGE,{"derivedFrom":subQ1})]})});}
            var Q4;
            {var subQ0=sQuery(id+"F0.wireOp",EDGE,"E25.0");var subQ1=sQuery(id+"F0.wireOp",EDGE,"E25.1");var subQ2=sQuery(id+"F0.wireOp",EDGE,"E25.2");var subQ3=sQuery(id+"F0.wireOp",EDGE,"E25.3");var subQ4=sQuery(id+"F0.wireOp",EDGE,"E25.4");var subQ5=sQuery(id+"F0.wireOp",EDGE,"E25.5");var subQ6=sQuery(id+"F0.wireOp",EDGE,"E25.6");var subQ7=sQuery(id+"F0.wireOp",EDGE,"E25.7");Q4=makeQuery(id+"F8.boolean.opBoolean","INTERSECT",EDGE,{"derivedFrom":[makeQuery(id+"F5.boolean.opBoolean","SPLIT",FACE,{"disambiguationData":[TD([makeQuery(id+"F2.opExtrude","SWEPT_FACE",FACE,{"disambiguationData":[OSD([subQ0])]})])],"derivedFrom":makeQuery(id+"F3.boolean.opBoolean","COPY",FACE,{"derivedFrom":makeQuery(id+"F3.opExtrude","CAP_FACE",FACE,{"disambiguationData":[OSD([subQ0,subQ1,subQ2,subQ3,subQ4,subQ5,subQ6,subQ7])],"isStart":false})})}),makeQuery(id+"F8.opExtrude","SWEPT_FACE",FACE,{"disambiguationData":[OSD([sQuery(id+"F7.wireOp",EDGE,"E67")])]})]});}
            var Q5;
            Q5=makeQuery(id+"F8.boolean.opBoolean","INTERSECT",EDGE,{"disambiguationData":[OD(0.0)],"derivedFrom":[makeQuery(id+"F5.opExtrude","SWEPT_FACE",FACE,{"disambiguationData":[OSD([sQuery(id+"F4.wireOp",EDGE,"E30")])]}),makeQuery(id+"F8.opExtrude","SWEPT_FACE",FACE,{"disambiguationData":[OSD([sQuery(id+"F7.wireOp",EDGE,"E67")])]})]});
            fillet(context, id + "F14", {"entities" : qUnion([Q0, Q1, Q2, Q3, Q4, Q5]), "radius" : 3 * mm, "tangentPropagation" : true, "allowEdgeOverflow" : false});
        }
        {
            var Q0;
            Q0=makeQuery(id+"F1.opExtrude","CAP_EDGE",EDGE,{"disambiguationData":[OSD([sQuery(id+"F0.wireOp",EDGE,"E1.bottom")])],"isStart":false});
            fillet(context, id + "F15", {"entities" : qUnion([Q0]), "radius" : 2 * mm, "tangentPropagation" : true, "allowEdgeOverflow" : false});
        }
        {
            var Q0;
            {var subQ0=sQuery(id+"F0.wireOp",EDGE,"E21.filletArc");var subQ1=sQuery(id+"F0.wireOp",EDGE,"E7");var subQ2=sQuery(id+"F0.wireOp",EDGE,"E6");var subQ3=sQuery(id+"F0.wireOp",EDGE,"E5");var subQ4=sQuery(id+"F0.wireOp",EDGE,"E4");var subQ5=sQuery(id+"F0.wireOp",EDGE,"E22.filletArc");var subQ6=sQuery(id+"F0.wireOp",EDGE,"E1.bottom");var subQ7=sQuery(id+"F0.wireOp",EDGE,"E1.right");var subQ8=sQuery(id+"F0.wireOp",EDGE,"E1.top");var subQ9=sQuery(id+"F0.wireOp",EDGE,"E1.left");var subQ10=sQuery(id+"F0.wireOp",EDGE,"E23.filletArc");var subQ11=sQuery(id+"F0.wireOp",EDGE,"E24.filletArc");Q0=makeQuery(id+"F2.boolean.opBoolean","SPLIT",FACE,{"disambiguationData":[TD([makeQuery(id+"F1.opExtrude","SWEPT_FACE",FACE,{"disambiguationData":[OSD([subQ6])]})])],"derivedFrom":makeQuery(id+"F1.opExtrude","CAP_FACE",FACE,{"disambiguationData":[OSD([subQ6,subQ8,subQ9,subQ7,subQ4,subQ3,subQ2,subQ1,subQ0,subQ5,subQ10,subQ11])],"isStart":true})});}
            var sketch = newSketch(context, id + "F16", { "sketchPlane" : qUnion([Q0])});
            skLineSegment(sketch, "E79", {"start": v(0, 80) * mm, "end": v(0, 110) * mm, "construction": true});
            skLineSegment(sketch, "E80", {"start": v(-33, 80) * mm, "end": v(-15, 98) * mm});
            skLineSegment(sketch, "E81", {"start": v(-15, 98) * mm, "end": v(-15, 110) * mm});
            skLineSegment(sketch, "E82", {"start": v(33, 80) * mm, "end": v(15, 98) * mm});
            skLineSegment(sketch, "E83", {"start": v(15, 98) * mm, "end": v(15, 110) * mm});
            skArc(sketch, "E84", {"start": v(15, 110) * mm, "mid": v(0, 125) * mm, "end": v(-15, 110) * mm});
            skCircle(sketch, "E85", {"center": v(0, 110) * mm, "radius": 6 * mm});
            skLineSegment(sketch, "E86", {"start": v(-44.25, 0) * mm, "end": v(90, 0) * mm, "construction": true});
            skLineSegment(sketch, "E87.MirrorCS", {"start": v(-15, -98) * mm, "end": v(-15, -110) * mm});
            skLineSegment(sketch, "E88.MirrorCS", {"start": v(15, -98) * mm, "end": v(15, -110) * mm});
            skCircle(sketch, "E89.MirrorC", {"center": v(0, -110) * mm, "radius": 6 * mm});
            skLineSegment(sketch, "E90.MirrorCS", {"start": v(-33, -80) * mm, "end": v(-15, -98) * mm});
            skLineSegment(sketch, "E91.MirrorCS", {"start": v(33, -80) * mm, "end": v(15, -98) * mm});
            skArc(sketch, "E92.MirrorCS", {"start": v(15, -110) * mm, "mid": v(0, -125) * mm, "end": v(-15, -110) * mm});
            skLineSegment(sketch, "E93.MirrorCS", {"start": v(0, -80) * mm, "end": v(0, -110) * mm, "construction": true});
            skSolve(sketch);
        }
        {
            var Q0;
            Q0=makeQuery(id+"F16.imprint","IMPRINT",FACE,{"disambiguationData":[TD([[makeQuery(id+"F16.imprint","IMPRINT",EDGE,{"derivedFrom":makeQuery(id+"F1.opExtrude","CAP_EDGE",EDGE,{"disambiguationData":[OSD([sQuery(id+"F0.wireOp",EDGE,"E1.left")])],"isStart":true})}),-1.0]])]});
            var Q1;
            Q1=makeQuery(id+"F16.imprint","IMPRINT",FACE,{"disambiguationData":[TD([[makeQuery(id+"F16.imprint","IMPRINT",EDGE,{"derivedFrom":sQuery(id+"F16.wireOp",EDGE,"E87.MirrorCS")}),1.0]])]});
            var Q2;
            {var subQ1=sQuery(id+"F16.wireOp",EDGE,"E80");Q2=makeQuery(id+"F16.imprint","IMPRINT",FACE,{"disambiguationData":[TD([[makeQuery(id+"F16.imprint","IMPRINT",EDGE,{"derivedFrom":subQ1}),-1.0]])]});}
            var Q3;
            Q3=makeQuery(id+"F2.opExtrude","CAP_FACE",FACE,{"disambiguationData":[OSD([sQuery(id+"F0.wireOp",EDGE,"E12"),sQuery(id+"F0.wireOp",EDGE,"E13"),sQuery(id+"F0.wireOp",EDGE,"E14"),sQuery(id+"F0.wireOp",EDGE,"E15"),sQuery(id+"F0.wireOp",EDGE,"E17.filletArc"),sQuery(id+"F0.wireOp",EDGE,"E18.filletArc"),sQuery(id+"F0.wireOp",EDGE,"E19.filletArc"),sQuery(id+"F0.wireOp",EDGE,"E20.filletArc"),sQuery(id+"F0.wireOp",EDGE,"E25.0"),sQuery(id+"F0.wireOp",EDGE,"E25.1"),sQuery(id+"F0.wireOp",EDGE,"E25.2"),sQuery(id+"F0.wireOp",EDGE,"E25.3"),sQuery(id+"F0.wireOp",EDGE,"E25.4"),sQuery(id+"F0.wireOp",EDGE,"E25.5"),sQuery(id+"F0.wireOp",EDGE,"E25.6"),sQuery(id+"F0.wireOp",EDGE,"E25.7")])],"isStart":false});
            extrude(context, id + "F17", {"entities" : qUnion([Q0, Q1, Q2]), "endBound" : BoundingType.UP_TO_SURFACE, "depth" : 25 * mm, "endBoundEntityFace" : qUnion([Q3]), "offsetDistance" : 25 * mm});
        }
    });
